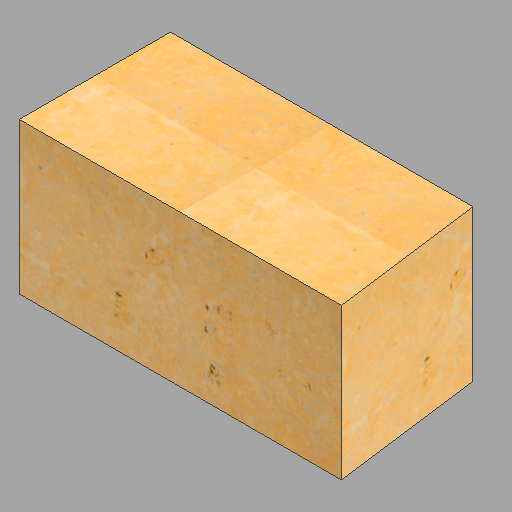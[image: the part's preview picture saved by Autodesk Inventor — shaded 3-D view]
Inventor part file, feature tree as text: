
AUTODESK INVENTOR PART (.ipt)
format: ipt  version: 2023 (Build 270158000, 158)  size: 377,344 bytes
history: native  units: in
note: dims shown in document units (in); Inventor stores cm internally (conversion verified against a paired STEP export)
features: extrude x1, sketch x1
ambient origin geometry x8: Origin, YZ Plane, XZ Plane, XY Plane, X Axis, Y Axis, Z Axis, Center Point
bodies: Solid1 (feature_tree)
feature tree (2):
  extrude  "Extrusion1"  Depth=24.0in
  sketch  "Sketch1"  dims[d0=48.0in d1=51.125in d2=24.0in d3=24.0in d4=0.0in]
